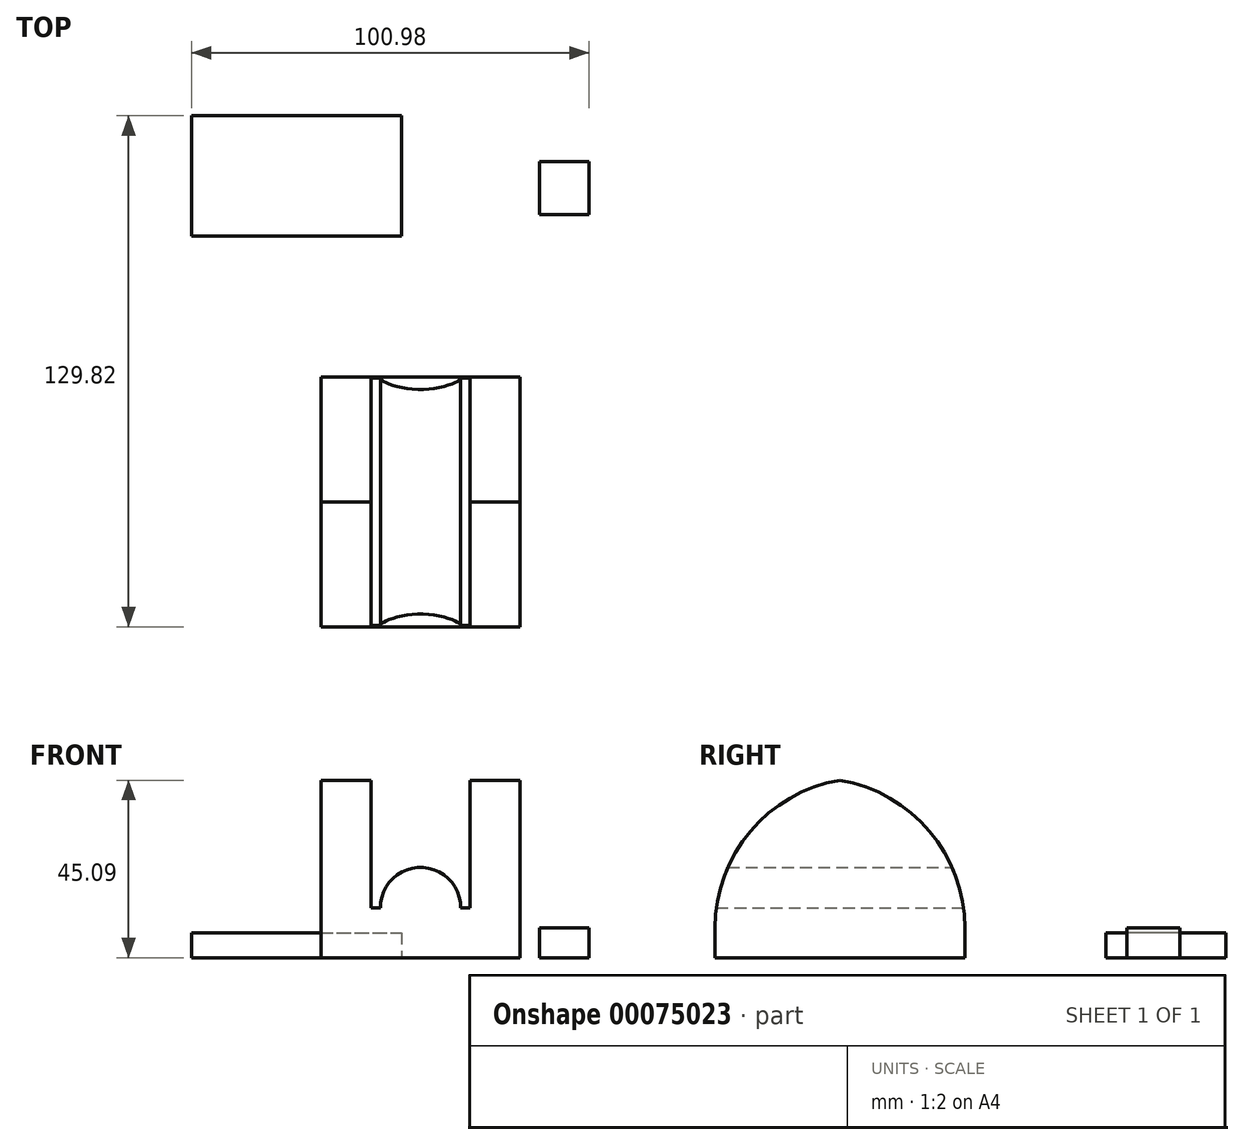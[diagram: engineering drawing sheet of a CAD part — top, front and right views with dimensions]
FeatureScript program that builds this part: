
annotation { "Feature Type Name" : "Feature", "Feature Type Description" : "" }
export const myFeature = defineFeature(function(context is Context, id is Id, definition is map)
    precondition{}
    {
        {
            var Q0;
            Q0=qCreatedBy(makeId("Front.planeOp"),FACE);
            var sketch = newSketch(context, id + "F0", { "sketchPlane" : qUnion([Q0])});
            skLineSegment(sketch, "E0", {"start": v(0, 0) * mm, "end": v(25.24, 0) * mm});
            skLineSegment(sketch, "E1", {"start": v(25.24, 0) * mm, "end": v(25.24, 45.63) * mm});
            skLineSegment(sketch, "E2", {"start": v(25.24, 45.63) * mm, "end": v(12.54, 45.63) * mm});
            skLineSegment(sketch, "E3", {"start": v(12.54, 45.63) * mm, "end": v(12.54, 12.7) * mm});
            skLineSegment(sketch, "E4", {"start": v(12.54, 12.7) * mm, "end": v(10.22, 12.7) * mm});
            skLineSegment(sketch, "E5.MirrorCS", {"start": v(-12.54, 45.63) * mm, "end": v(-12.54, 12.7) * mm});
            skLineSegment(sketch, "E6.MirrorCS", {"start": v(-25.24, 45.63) * mm, "end": v(-12.54, 45.63) * mm});
            skLineSegment(sketch, "E7.MirrorCS", {"start": v(-25.24, 0) * mm, "end": v(-25.24, 45.63) * mm});
            skLineSegment(sketch, "E8.MirrorCS", {"start": v(-12.54, 12.7) * mm, "end": v(-10.22, 12.7) * mm});
            skLineSegment(sketch, "E9.MirrorCS", {"start": v(0, 0) * mm, "end": v(-25.24, 0) * mm});
            skArc(sketch, "E10", {"start": v(10.22, 12.7) * mm, "mid": v(0, 22.92) * mm, "end": v(-10.22, 12.7) * mm});
            skSolve(sketch);
        }
        {
            var Q0;
            Q0=makeQuery(id+"F0.imprint","IMPRINT",FACE,{"disambiguationData":[TD([[makeQuery(id+"F0.imprint","IMPRINT",EDGE,{"derivedFrom":sQuery(id+"F0.wireOp",EDGE,"E0")}),1.0]])]});
            extrude(context, id + "F1", {"entities" : qUnion([Q0]), "depth" : 63.5 * mm});
        }
        {
            var Q0;
            Q0=makeQuery(id+"F1.opExtrude","CAP_EDGE",EDGE,{"disambiguationData":[OSD([sQuery(id+"F0.wireOp",EDGE,"E6.MirrorCS")])],"isStart":false});
            var Q1;
            Q1=makeQuery(id+"F1.opExtrude","CAP_EDGE",EDGE,{"disambiguationData":[OSD([sQuery(id+"F0.wireOp",EDGE,"E6.MirrorCS")])],"isStart":true});
            var Q2;
            Q2=makeQuery(id+"F1.opExtrude","CAP_EDGE",EDGE,{"disambiguationData":[OSD([sQuery(id+"F0.wireOp",EDGE,"E2")])],"isStart":false});
            var Q3;
            Q3=makeQuery(id+"F1.opExtrude","CAP_EDGE",EDGE,{"disambiguationData":[OSD([sQuery(id+"F0.wireOp",EDGE,"E2")])],"isStart":true});
            fillet(context, id + "F2", {"entities" : qUnion([Q0, Q1, Q2, Q3]), "radius" : 38.1 * mm, "tangentPropagation" : true, "allowEdgeOverflow" : false});
        }
        {
            var Q0;
            Q0=qCreatedBy(makeId("Front.planeOp"),FACE);
            var sketch = newSketch(context, id + "F3", { "sketchPlane" : qUnion([Q0])});
            skLineSegment(sketch, "E11", {"start": v(48.58, 0) * mm, "end": v(48.58, 44.78) * mm});
            skLineSegment(sketch, "E12", {"start": v(48.58, 44.78) * mm, "end": v(63.79, 44.78) * mm});
            skLineSegment(sketch, "E13", {"start": v(63.79, 44.78) * mm, "end": v(48.58, 0) * mm});
            skSolve(sketch);
        }
        {
            var Q0;
            Q0=sQuery(id+"F3.wireOp",EDGE,"E12");
            var Q1;
            Q1=sQuery(id+"F3.wireOp",EDGE,"E11");
            var Q2;
            Q2=sQuery(id+"F3.wireOp",EDGE,"E13");
            extrude(context, id + "F4", {"bodyType" : ToolBodyType.SURFACE, "surfaceEntities" : qUnion([Q0, Q1, Q2]), "depth" : 76.2 * mm});
        }
        {
            var Q0;
            Q0=qCreatedBy(makeId("Top.planeOp"),FACE);
            var sketch = newSketch(context, id + "F5", { "sketchPlane" : qUnion([Q0])});
            skLineSegment(sketch, "E14.bottom", {"start": v(-58.19, 66.32) * mm, "end": v(-4.85, 66.32) * mm});
            skLineSegment(sketch, "E14.top", {"start": v(-58.19, 35.8) * mm, "end": v(-4.85, 35.8) * mm});
            skLineSegment(sketch, "E14.left", {"start": v(-58.19, 66.32) * mm, "end": v(-58.19, 35.8) * mm});
            skLineSegment(sketch, "E14.right", {"start": v(-4.85, 66.32) * mm, "end": v(-4.85, 35.8) * mm});
            skSolve(sketch);
        }
        {
            var Q0;
            Q0 = qSketchRegion(id + "F5", true);
            extrude(context, id + "F6", {"entities" : qUnion([Q0]), "depth" : 6.35 * mm});
        }
        {
            var Q0;
            Q0=qCreatedBy(makeId("Top.planeOp"),FACE);
            var sketch = newSketch(context, id + "F7", { "sketchPlane" : qUnion([Q0])});
            skLineSegment(sketch, "E15.bottom", {"start": v(30.24, 54.62) * mm, "end": v(42.79, 54.62) * mm});
            skLineSegment(sketch, "E15.top", {"start": v(30.24, 41.22) * mm, "end": v(42.79, 41.22) * mm});
            skLineSegment(sketch, "E15.left", {"start": v(30.24, 54.62) * mm, "end": v(30.24, 41.22) * mm});
            skLineSegment(sketch, "E15.right", {"start": v(42.79, 54.62) * mm, "end": v(42.79, 41.22) * mm});
            skSolve(sketch);
        }
        {
            var Q0;
            Q0 = qSketchRegion(id + "F7", true);
            extrude(context, id + "F8", {"entities" : qUnion([Q0]), "depth" : 7.62 * mm});
        }
    });
